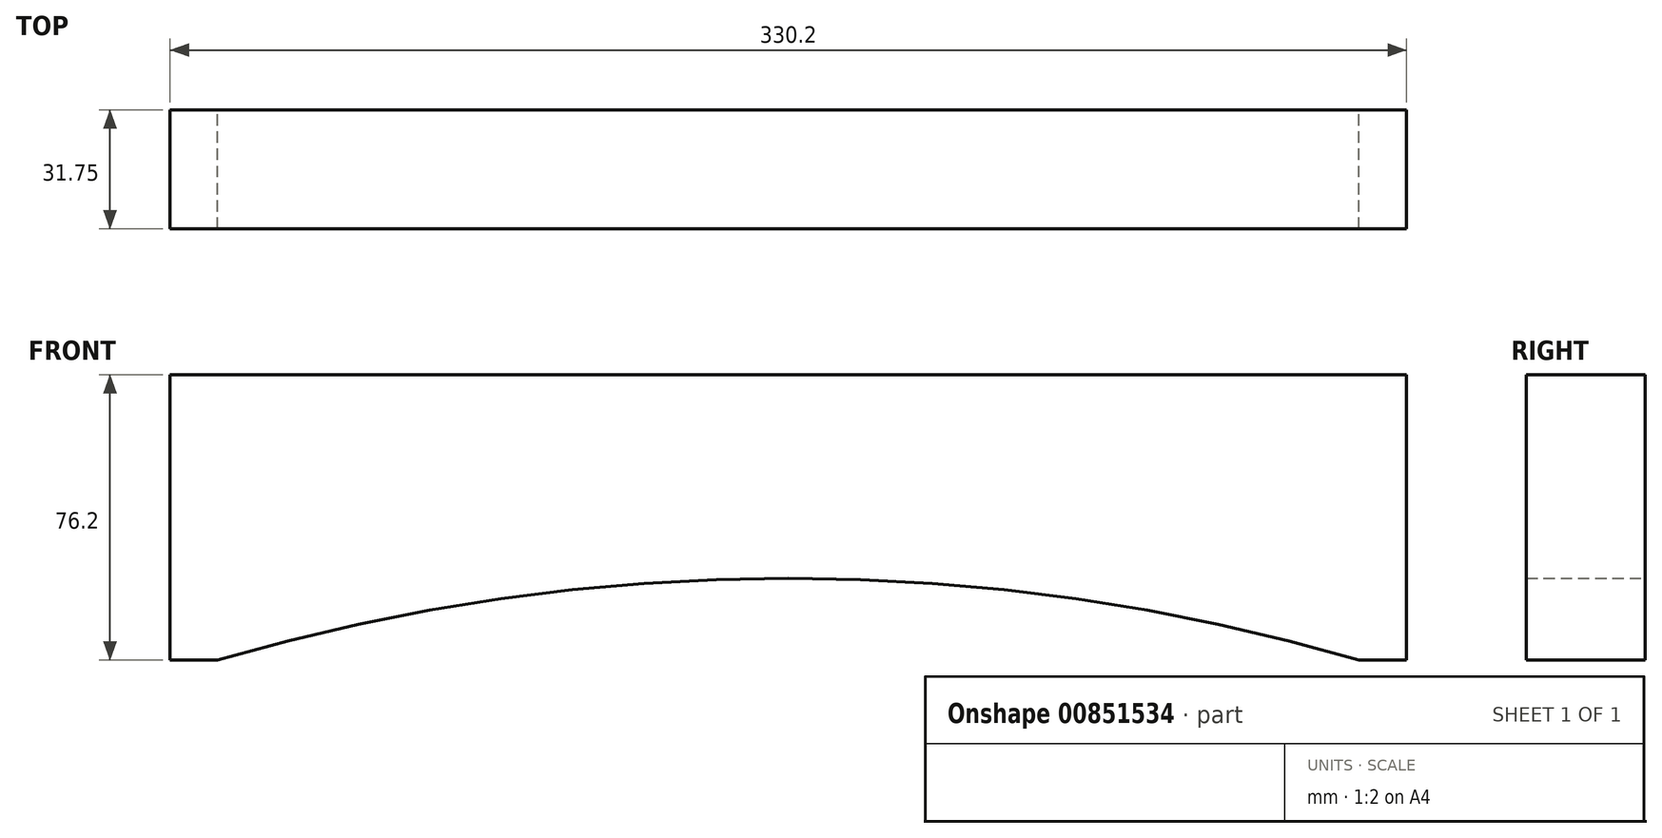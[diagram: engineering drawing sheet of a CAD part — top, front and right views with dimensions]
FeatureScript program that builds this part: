
annotation { "Feature Type Name" : "Feature", "Feature Type Description" : "" }
export const myFeature = defineFeature(function(context is Context, id is Id, definition is map)
    precondition{}
    {
        {
            var Q0;
            Q0=qCreatedBy(makeId("Front.planeOp"),FACE);
            var sketch = newSketch(context, id + "F0", { "sketchPlane" : qUnion([Q0])});
            skLineSegment(sketch, "E0", {"start": v(94.48, 25.21) * mm, "end": v(-235.72, 25.21) * mm});
            skLineSegment(sketch, "E1", {"start": v(-235.72, 25.21) * mm, "end": v(-235.72, -50.99) * mm});
            skLineSegment(sketch, "E2", {"start": v(-235.72, -50.99) * mm, "end": v(-223.02, -50.99) * mm});
            skLineSegment(sketch, "E3", {"start": v(94.48, 25.21) * mm, "end": v(94.48, -50.99) * mm});
            skLineSegment(sketch, "E4", {"start": v(94.48, -50.99) * mm, "end": v(81.78, -50.99) * mm});
            skArc(sketch, "E5", {"start": v(81.78, -50.99) * mm, "mid": v(-70.62, -29.14) * mm, "end": v(-223.02, -50.99) * mm});
            skSolve(sketch);
        }
        {
            var Q0;
            Q0 = qSketchRegion(id + "F0", true);
            extrude(context, id + "F1", {"entities" : qUnion([Q0]), "depth" : 31.75 * mm, "offsetDistance" : 25.4 * mm});
        }
    });
